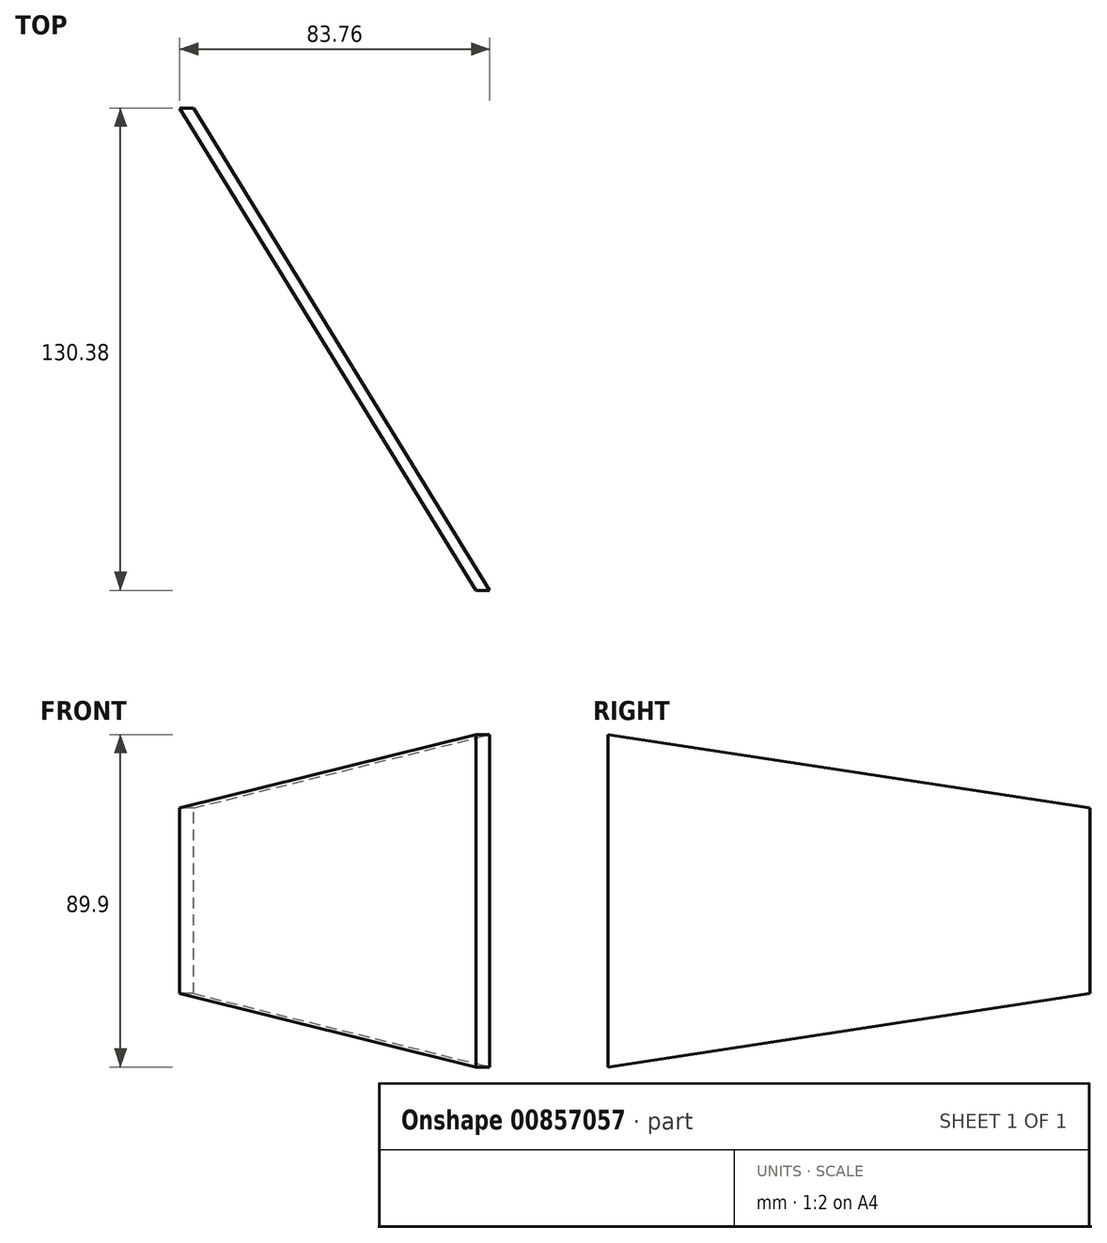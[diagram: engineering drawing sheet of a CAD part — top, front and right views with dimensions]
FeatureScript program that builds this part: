
annotation { "Feature Type Name" : "Feature", "Feature Type Description" : "" }
export const myFeature = defineFeature(function(context is Context, id is Id, definition is map)
    precondition{}
    {
        {
            var Q0;
            Q0=qCreatedBy(makeId("Right.planeOp"),FACE);
            var sketch = newSketch(context, id + "F0", { "sketchPlane" : qUnion([Q0])});
            skLineSegment(sketch, "E0", {"start": v(0, 48.82) * mm, "end": v(0, -48.82) * mm});
            skLineSegment(sketch, "E1", {"start": v(25.4, 44.95) * mm, "end": v(25.4, -44.95) * mm});
            skLineSegment(sketch, "E2", {"start": v(155.78, 25.1) * mm, "end": v(155.78, -25.1) * mm});
            skCircle(sketch, "E3", {"center": v(311.35, 0) * mm, "radius": 1.39 * mm});
            skLineSegment(sketch, "E4", {"start": v(0, 48.82) * mm, "end": v(311.56, 1.37) * mm});
            skLineSegment(sketch, "E5", {"start": v(0, -48.82) * mm, "end": v(311.56, -1.37) * mm});
            skSolve(sketch);
        }
        {
            var Q0;
            {var subQ5=sQuery(id+"F0.wireOp",EDGE,"E2");Q0=makeQuery(id+"F0.imprint","IMPRINT",FACE,{"disambiguationData":[TD([[makeQuery(id+"F0.imprint","IMPRINT",EDGE,{"derivedFrom":subQ5}),-1.0]])]});}
            extrude(context, id + "F1", {"entities" : qUnion([Q0]), "depth" : 254 * mm, "offsetDistance" : 25.4 * mm, "symmetric" : true});
        }
        {
            var Q0;
            Q0=qCreatedBy(makeId("Top.planeOp"),FACE);
            var sketch = newSketch(context, id + "F2", { "sketchPlane" : qUnion([Q0])});
            skLineSegment(sketch, "E6", {"start": v(-182.56, 291.34) * mm, "end": v(182.56, 291.34) * mm});
            skLineSegment(sketch, "E7", {"start": v(0, 0) * mm, "end": v(0, 291.34) * mm});
            skLineSegment(sketch, "E8", {"start": v(-182.56, 291.34) * mm, "end": v(-3.73, 0) * mm});
            skLineSegment(sketch, "E9", {"start": v(0, 0) * mm, "end": v(-178.84, 291.34) * mm});
            skLineSegment(sketch, "E10", {"start": v(-3.73, 0) * mm, "end": v(0, 0) * mm});
            skSolve(sketch);
        }
        {
            var Q0;
            {var subQ0=sQuery(id+"F2.wireOp",EDGE,"E8");Q0=makeQuery(id+"F2.imprint","IMPRINT",FACE,{"disambiguationData":[TD([[makeQuery(id+"F2.imprint","IMPRINT",EDGE,{"derivedFrom":subQ0}),1.0]])]});}
            extrude(context, id + "F3", {"entities" : qUnion([Q0]), "operationType" : NewBodyOperationType.INTERSECT, "depth" : 101.6 * mm, "offsetDistance" : 25.4 * mm, "symmetric" : true});
        }
    });
